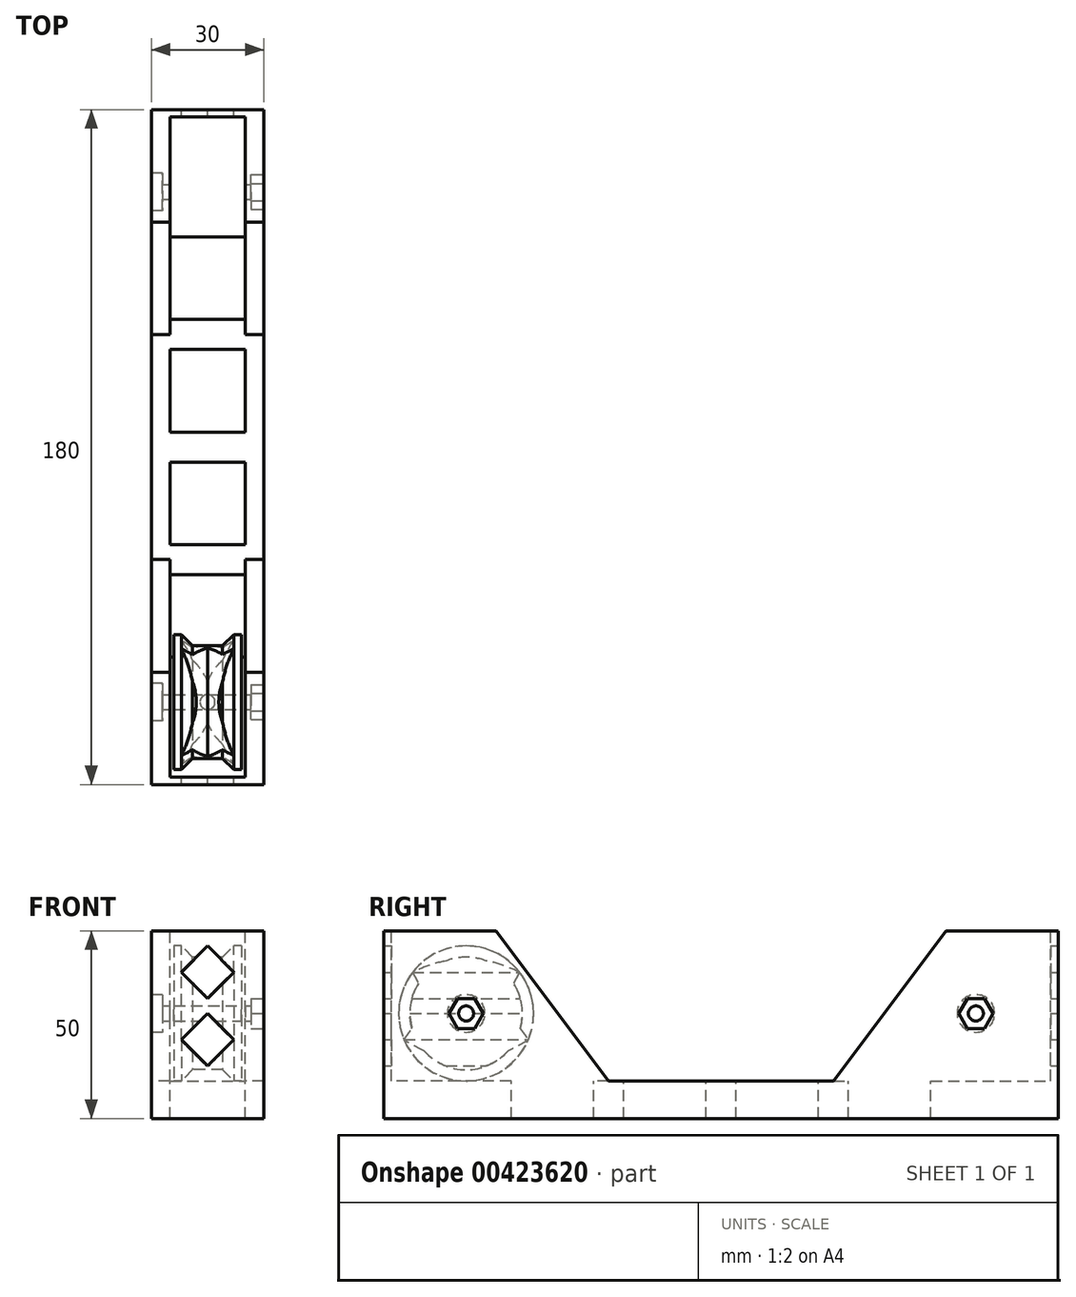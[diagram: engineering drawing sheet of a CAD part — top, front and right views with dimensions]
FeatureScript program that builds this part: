
annotation { "Feature Type Name" : "Feature", "Feature Type Description" : "" }
export const myFeature = defineFeature(function(context is Context, id is Id, definition is map)
    precondition{}
    {
        {
            var Q0;
            Q0=qCreatedBy(makeId("Right.planeOp"),FACE);
            var sketch = newSketch(context, id + "F0", { "sketchPlane" : qUnion([Q0])});
            skLineSegment(sketch, "E0", {"start": v(0, 0) * mm, "end": v(-90, 0) * mm});
            skLineSegment(sketch, "E1", {"start": v(-90, 0) * mm, "end": v(-90, 50) * mm});
            skLineSegment(sketch, "E2", {"start": v(-90, 50) * mm, "end": v(-60, 50) * mm});
            skLineSegment(sketch, "E3", {"start": v(-60, 50) * mm, "end": v(-30, 10) * mm});
            skLineSegment(sketch, "E4", {"start": v(-30, 10) * mm, "end": v(0, 10) * mm});
            skLineSegment(sketch, "E5.MirrorCS", {"start": v(30, 10) * mm, "end": v(0, 10) * mm});
            skLineSegment(sketch, "E6.MirrorCS", {"start": v(0, 0) * mm, "end": v(90, 0) * mm});
            skLineSegment(sketch, "E7.MirrorCS", {"start": v(90, 0) * mm, "end": v(90, 50) * mm});
            skLineSegment(sketch, "E8.MirrorCS", {"start": v(90, 50) * mm, "end": v(60, 50) * mm});
            skLineSegment(sketch, "E9.MirrorCS", {"start": v(60, 50) * mm, "end": v(30, 10) * mm});
            skPoint(sketch, "E10", {"position": v(-68, 28) * mm});
            skLineSegment(sketch, "E11", {"start": v(-68, 50) * mm, "end": v(-68, 0) * mm, "construction": true});
            skPoint(sketch, "E12.MirrorP", {"position": v(68, 28) * mm});
            skCircle(sketch, "E13", {"center": v(0, 120.74) * mm, "radius": 100 * mm, "construction": true});
            skCircle(sketch, "E14", {"center": v(-68, 28) * mm, "radius": 15 * mm});
            skSolve(sketch);
        }
        {
            var Q0;
            Q0=makeQuery(id+"F0.imprint","IMPRINT",FACE,{"disambiguationData":[TD([[makeQuery(id+"F0.imprint","IMPRINT",EDGE,{"derivedFrom":sQuery(id+"F0.wireOp",EDGE,"E0")}),-1.0]])]});
            var Q1;
            Q1=makeQuery(id+"F0.imprint","IMPRINT",FACE,{"disambiguationData":[TD([[makeQuery(id+"F0.imprint","IMPRINT",EDGE,{"derivedFrom":sQuery(id+"F0.wireOp",EDGE,"E14")}),1.0]])]});
            extrude(context, id + "F1", {"entities" : qUnion([Q0, Q1]), "endBound" : BoundingType.SYMMETRIC, "depth" : 30 * mm, "offsetDistance" : 25 * mm});
        }
        {
            var Q0;
            Q0=makeQuery(id+"F1.opExtrude","SWEPT_FACE",FACE,{"disambiguationData":[OSD([sQuery(id+"F0.wireOp",EDGE,"E2")])]});
            var sketch = newSketch(context, id + "F2", { "sketchPlane" : qUnion([Q0])});
            skLineSegment(sketch, "E15", {"start": v(-10, -30) * mm, "end": v(-10, -88) * mm});
            skLineSegment(sketch, "E16.MirrorCS", {"start": v(10, -30) * mm, "end": v(10, -88) * mm});
            skLineSegment(sketch, "E17.MirrorCS", {"start": v(10, 30) * mm, "end": v(10, 88) * mm});
            skLineSegment(sketch, "E18.MirrorCS", {"start": v(-10, 30) * mm, "end": v(-10, 88) * mm});
            skLineSegment(sketch, "E19", {"start": v(-10, -30) * mm, "end": v(10, -30) * mm});
            skLineSegment(sketch, "E20", {"start": v(-10, -88) * mm, "end": v(-11, -88) * mm});
            skLineSegment(sketch, "E21.MirrorCS", {"start": v(-10, 30) * mm, "end": v(10, 30) * mm});
            skLineSegment(sketch, "E22.MirrorCS", {"start": v(-11, 88) * mm, "end": v(-10, 88) * mm});
            skLineSegment(sketch, "E23", {"start": v(-10, -88) * mm, "end": v(10, -88) * mm});
            skLineSegment(sketch, "E24.MirrorCS", {"start": v(-10, 88) * mm, "end": v(10, 88) * mm});
            skSolve(sketch);
        }
        {
            var Q0;
            {var subQ0=sQuery(id+"F2.wireOp",EDGE,"E19");Q0=makeQuery(id+"F2.imprint","IMPRINT",FACE,{"disambiguationData":[TD([[makeQuery(id+"F2.imprint","IMPRINT",EDGE,{"derivedFrom":subQ0}),-1.0]])]});}
            var Q1;
            {var subQ0=sQuery(id+"F2.wireOp",EDGE,"E20");Q1=makeQuery(id+"F2.imprint","IMPRINT",FACE,{"disambiguationData":[TD([[makeQuery(id+"F2.imprint","IMPRINT",EDGE,{"derivedFrom":subQ0}),-1.0]])]});}
            var Q2;
            Q2=makeQuery(id+"F1.opExtrude","SWEPT_FACE",FACE,{"disambiguationData":[OSD([sQuery(id+"F0.wireOp",EDGE,"E0"),sQuery(id+"F0.wireOp",EDGE,"E6.MirrorCS")])]});
            extrude(context, id + "F3", {"entities" : qUnion([Q0, Q1]), "operationType" : NewBodyOperationType.REMOVE, "endBound" : BoundingType.UP_TO_SURFACE, "oppositeDirection" : true, "depth" : 25 * mm, "endBoundEntityFace" : qUnion([Q2]), "hasOffset" : true, "offsetDistance" : 10 * mm});
        }
        {
            var Q0;
            Q0=makeQuery(id+"F2.imprint","IMPRINT",FACE,{"disambiguationData":[TD([[makeQuery(id+"F2.imprint","IMPRINT",EDGE,{"derivedFrom":sQuery(id+"F2.wireOp",EDGE,"E17.MirrorCS")}),1.0]])]});
            var Q1;
            {var subQ0=sQuery(id+"F2.wireOp",EDGE,"E23");Q1=makeQuery(id+"F2.imprint","IMPRINT",FACE,{"disambiguationData":[TD([[makeQuery(id+"F2.imprint","IMPRINT",EDGE,{"derivedFrom":subQ0}),1.0]])]});}
            var Q2;
            Q2=makeQuery(id+"F1.opExtrude","SWEPT_FACE",FACE,{"disambiguationData":[OSD([sQuery(id+"F0.wireOp",EDGE,"E0"),sQuery(id+"F0.wireOp",EDGE,"E6.MirrorCS")])]});
            extrude(context, id + "F4", {"entities" : qUnion([Q0, Q1]), "operationType" : NewBodyOperationType.REMOVE, "endBound" : BoundingType.UP_TO_SURFACE, "oppositeDirection" : true, "depth" : 25 * mm, "endBoundEntityFace" : qUnion([Q2]), "hasOffset" : true, "offsetDistance" : 10 * mm});
        }
        {
            var Q0;
            Q0=sQuery(id+"F0.wireOp",VERTEX,"E10");
            var Q1;
            Q1=makeQuery(id+"F1.opExtrude","SWEPT_FACE",FACE,{"disambiguationData":[OSD([sQuery(id+"F0.wireOp",EDGE,"E1")])]});
            cPlane(context, id + "F5", {"entities" : qUnion([Q0, Q1]), "cplaneType" : CPlaneType.PLANE_POINT, "offset" : 25 * mm, "width" : 150 * mm, "height" : 150 * mm});
        }
        {
            var Q0;
            Q0=qCreatedBy(id+"F5.planeOp",FACE);
            var sketch = newSketch(context, id + "F6", { "sketchPlane" : qUnion([Q0])});
            skLineSegment(sketch, "E25.0", {"start": v(0, 43) * mm, "end": v(0, 13) * mm, "construction": true});
            skLineSegment(sketch, "E26", {"start": v(0, 43) * mm, "end": v(-4, 43) * mm});
            skLineSegment(sketch, "E27", {"start": v(-4, 43) * mm, "end": v(-7, 46) * mm});
            skLineSegment(sketch, "E28", {"start": v(-7, 46) * mm, "end": v(-9, 46) * mm});
            skLineSegment(sketch, "E29", {"start": v(-9, 46) * mm, "end": v(-9, 28) * mm});
            skPoint(sketch, "E29.endSnap0", {"position": v(0, 28) * mm});
            skLineSegment(sketch, "E30.MirrorCS", {"start": v(0, 43) * mm, "end": v(4, 43) * mm});
            skLineSegment(sketch, "E31.MirrorCS", {"start": v(4, 43) * mm, "end": v(7, 46) * mm});
            skLineSegment(sketch, "E32.MirrorCS", {"start": v(7, 46) * mm, "end": v(9, 46) * mm});
            skLineSegment(sketch, "E33.MirrorCS", {"start": v(9, 46) * mm, "end": v(9, 28) * mm});
            skLineSegment(sketch, "E34", {"start": v(-9, 28) * mm, "end": v(0, 28) * mm});
            skLineSegment(sketch, "E35.MirrorCS", {"start": v(9, 28) * mm, "end": v(0, 28) * mm});
            skSolve(sketch);
        }
        {
            var Q0;
            Q0 = qSketchRegion(id + "F6", true);
            var Q1;
            Q1=sQuery(id+"F6.wireOp",EDGE,"E34");
            revolve(context, id + "F7", {"entities" : qUnion([Q0]), "axis" : qUnion([Q1]), "revolveType" : RevolveType.FULL});
        }
        {
            var Q0;
            Q0=makeQuery(id+"F1.opExtrude","CAP_FACE",FACE,{"disambiguationData":[OSD([sQuery(id+"F0.wireOp",EDGE,"E0"),sQuery(id+"F0.wireOp",EDGE,"E1"),sQuery(id+"F0.wireOp",EDGE,"E2"),sQuery(id+"F0.wireOp",EDGE,"E3"),sQuery(id+"F0.wireOp",EDGE,"E4"),sQuery(id+"F0.wireOp",EDGE,"E5.MirrorCS"),sQuery(id+"F0.wireOp",EDGE,"E6.MirrorCS"),sQuery(id+"F0.wireOp",EDGE,"E7.MirrorCS"),sQuery(id+"F0.wireOp",EDGE,"E8.MirrorCS"),sQuery(id+"F0.wireOp",EDGE,"E9.MirrorCS")])],"isStart":false});
            var sketch = newSketch(context, id + "F8", { "sketchPlane" : qUnion([Q0])});
            skPoint(sketch, "E36.0", {"position": v(-68, 28) * mm});
            skPoint(sketch, "E37.0", {"position": v(68, 28) * mm});
            skCircle(sketch, "E38.cCircle", {"center": v(-68, 28) * mm, "radius": 4 * mm, "construction": true});
            skLineSegment(sketch, "E38.0", {"start": v(-65.7, 24) * mm, "end": v(-70.3, 24) * mm});
            skLineSegment(sketch, "E38.1", {"start": v(-70.3, 24) * mm, "end": v(-72.62, 28) * mm});
            skLineSegment(sketch, "E38.2", {"start": v(-72.62, 28) * mm, "end": v(-70.3, 32) * mm});
            skLineSegment(sketch, "E38.3", {"start": v(-70.3, 32) * mm, "end": v(-65.7, 32) * mm});
            skLineSegment(sketch, "E38.4", {"start": v(-65.7, 32) * mm, "end": v(-63.38, 28) * mm});
            skLineSegment(sketch, "E38.5", {"start": v(-63.38, 28) * mm, "end": v(-65.7, 24) * mm});
            skPoint(sketch, "E38.0.midPoint", {"position": v(-68, 24) * mm});
            skLineSegment(sketch, "E39.MirrorCS", {"start": v(65.7, 32) * mm, "end": v(63.38, 28) * mm});
            skLineSegment(sketch, "E40.MirrorCS", {"start": v(70.3, 32) * mm, "end": v(65.7, 32) * mm});
            skLineSegment(sketch, "E41.MirrorCS", {"start": v(72.62, 28) * mm, "end": v(70.3, 32) * mm});
            skLineSegment(sketch, "E42.MirrorCS", {"start": v(70.3, 24) * mm, "end": v(72.62, 28) * mm});
            skLineSegment(sketch, "E43.MirrorCS", {"start": v(65.7, 24) * mm, "end": v(70.3, 24) * mm});
            skLineSegment(sketch, "E44.MirrorCS", {"start": v(63.38, 28) * mm, "end": v(65.7, 24) * mm});
            skSolve(sketch);
        }
        {
            var Q0;
            Q0=sQuery(id+"F8.wireOp",VERTEX,"E36.0");
            var Q1;
            Q1=sQuery(id+"F8.wireOp",VERTEX,"E37.0");
            var Q2;
            Q2=makeQuery(id+"F1.opExtrude","SWEPT_BODY",BODY,{"disambiguationData":[OSD([sQuery(id+"F0.wireOp",EDGE,"E0"),sQuery(id+"F0.wireOp",EDGE,"E1"),sQuery(id+"F0.wireOp",EDGE,"E2"),sQuery(id+"F0.wireOp",EDGE,"E3"),sQuery(id+"F0.wireOp",EDGE,"E4"),sQuery(id+"F0.wireOp",EDGE,"E5.MirrorCS"),sQuery(id+"F0.wireOp",EDGE,"E6.MirrorCS"),sQuery(id+"F0.wireOp",EDGE,"E7.MirrorCS"),sQuery(id+"F0.wireOp",EDGE,"E8.MirrorCS"),sQuery(id+"F0.wireOp",EDGE,"E9.MirrorCS")])]});
            var Q3;
            Q3=makeQuery(id+"F7.opRevolve","SWEPT_BODY",BODY,{"disambiguationData":[OSD([sQuery(id+"F6.wireOp",EDGE,"E26"),sQuery(id+"F6.wireOp",EDGE,"E27"),sQuery(id+"F6.wireOp",EDGE,"E28"),sQuery(id+"F6.wireOp",EDGE,"E29"),sQuery(id+"F6.wireOp",EDGE,"E30.MirrorCS"),sQuery(id+"F6.wireOp",EDGE,"E31.MirrorCS"),sQuery(id+"F6.wireOp",EDGE,"E32.MirrorCS"),sQuery(id+"F6.wireOp",EDGE,"E33.MirrorCS"),sQuery(id+"F6.wireOp",EDGE,"E34"),sQuery(id+"F6.wireOp",EDGE,"E35.MirrorCS")])]});
            hole(context, id + "F9", {"style" : HoleStyle.SIMPLE, "endStyle" : HoleEndStyle.THROUGH, "holeDiameter" : 4 * mm, "isTappedThrough" : true, "tappedDepth" : 6 * mm, "tapClearance" : 3, "locations" : qUnion([Q0, Q1]), "scope" : qUnion([Q2, Q3])});
        }
        {
            var Q0;
            {var subQ0=sQuery(id+"F0.wireOp",EDGE,"E6.MirrorCS");var subQ1=sQuery(id+"F0.wireOp",EDGE,"E0");Q0=makeQuery(id+"F4.boolean.opBoolean","MERGE",FACE,{"derivedFrom":[makeQuery(id+"F3.boolean.opBoolean","MERGE",FACE,{"derivedFrom":[makeQuery(id+"F1.opExtrude","SWEPT_FACE",FACE,{"disambiguationData":[OSD([sQuery(id+"F0.wireOp",EDGE,"E4"),sQuery(id+"F0.wireOp",EDGE,"E5.MirrorCS")])]}),makeQuery(id+"F3.opExtrude","CAP_FACE",FACE,{"disambiguationData":[OSD([subQ1,subQ0])],"isStart":false})]}),makeQuery(id+"F4.opExtrude","CAP_FACE",FACE,{"disambiguationData":[OSD([subQ1,subQ0])],"isStart":false})]});}
            var sketch = newSketch(context, id + "F10", { "sketchPlane" : qUnion([Q0])});
            skPoint(sketch, "E45.middle", {"position": v(0, 0) * mm});
            skLineSegment(sketch, "E46.bottom", {"start": v(-10, 26) * mm, "end": v(10, 26) * mm});
            skLineSegment(sketch, "E46.top", {"start": v(-10, 4) * mm, "end": v(10, 4) * mm});
            skLineSegment(sketch, "E46.left", {"start": v(-10, 26) * mm, "end": v(-10, 4) * mm});
            skLineSegment(sketch, "E46.right", {"start": v(10, 26) * mm, "end": v(10, 4) * mm});
            skPoint(sketch, "E46.middle", {"position": v(0, 15) * mm});
            skLineSegment(sketch, "E47.MirrorCS", {"start": v(-10, -4) * mm, "end": v(10, -4) * mm});
            skLineSegment(sketch, "E48.MirrorCS", {"start": v(10, -26) * mm, "end": v(10, -4) * mm});
            skLineSegment(sketch, "E49.MirrorCS", {"start": v(-10, -26) * mm, "end": v(10, -26) * mm});
            skLineSegment(sketch, "E50.MirrorCS", {"start": v(-10, -26) * mm, "end": v(-10, -4) * mm});
            skLineSegment(sketch, "E51", {"start": v(15, -30) * mm, "end": v(-15, -30) * mm, "construction": true});
            skLineSegment(sketch, "E52.MirrorCS", {"start": v(-10, -34) * mm, "end": v(10, -34) * mm});
            skLineSegment(sketch, "E53.MirrorCS", {"start": v(10, -34) * mm, "end": v(10, -56) * mm});
            skLineSegment(sketch, "E54.MirrorCS", {"start": v(-10, -56) * mm, "end": v(10, -56) * mm});
            skLineSegment(sketch, "E55.MirrorCS", {"start": v(-10, -34) * mm, "end": v(-10, -56) * mm});
            skLineSegment(sketch, "E56.MirrorCS", {"start": v(-10, 34) * mm, "end": v(10, 34) * mm});
            skLineSegment(sketch, "E57.MirrorCS", {"start": v(-10, 56) * mm, "end": v(10, 56) * mm});
            skLineSegment(sketch, "E58.MirrorCS", {"start": v(10, 34) * mm, "end": v(10, 56) * mm});
            skLineSegment(sketch, "E59.MirrorCS", {"start": v(-10, 34) * mm, "end": v(-10, 56) * mm});
            skSolve(sketch);
        }
        {
            var Q0;
            Q0 = qSketchRegion(id + "F10", true);
            var Q1;
            Q1=makeQuery(id+"F1.opExtrude","SWEPT_FACE",FACE,{"disambiguationData":[OSD([sQuery(id+"F0.wireOp",EDGE,"E0"),sQuery(id+"F0.wireOp",EDGE,"E6.MirrorCS")])]});
            extrude(context, id + "F11", {"entities" : qUnion([Q0]), "operationType" : NewBodyOperationType.REMOVE, "endBound" : BoundingType.UP_TO_SURFACE, "oppositeDirection" : true, "depth" : 25 * mm, "endBoundEntityFace" : qUnion([Q1]), "offsetDistance" : 25 * mm});
        }
        {
            var Q0;
            Q0=makeQuery(id+"F8.imprint","IMPRINT",FACE,{"disambiguationData":[TD([[makeQuery(id+"F8.imprint","IMPRINT",EDGE,{"derivedFrom":sQuery(id+"F8.wireOp",EDGE,"E38.0")}),-1.0]])]});
            var Q1;
            Q1=makeQuery(id+"F8.imprint","IMPRINT",FACE,{"disambiguationData":[TD([[makeQuery(id+"F8.imprint","IMPRINT",EDGE,{"derivedFrom":sQuery(id+"F8.wireOp",EDGE,"E39.MirrorCS")}),1.0]])]});
            var Q2;
            {var subQ0=sQuery(id+"F2.wireOp",EDGE,"E16.MirrorCS");Q2=makeQuery(id+"F4.boolean.opBoolean","MERGE",FACE,{"derivedFrom":[makeQuery(id+"F3.boolean.opBoolean","COPY",FACE,{"derivedFrom":makeQuery(id+"F3.opExtrude","SWEPT_FACE",FACE,{"disambiguationData":[OSD([subQ0])]})}),makeQuery(id+"F4.opExtrude","SWEPT_FACE",FACE,{"disambiguationData":[OSD([subQ0])]})]});}
            extrude(context, id + "F12", {"entities" : qUnion([Q0, Q1]), "operationType" : NewBodyOperationType.REMOVE, "endBound" : BoundingType.UP_TO_SURFACE, "oppositeDirection" : true, "depth" : 25 * mm, "endBoundEntityFace" : qUnion([Q2]), "hasOffset" : true, "offsetDistance" : 1.6 * mm});
        }
        {
            var Q0;
            Q0=makeQuery(id+"F1.opExtrude","CAP_FACE",FACE,{"disambiguationData":[OSD([sQuery(id+"F0.wireOp",EDGE,"E0"),sQuery(id+"F0.wireOp",EDGE,"E1"),sQuery(id+"F0.wireOp",EDGE,"E2"),sQuery(id+"F0.wireOp",EDGE,"E3"),sQuery(id+"F0.wireOp",EDGE,"E4"),sQuery(id+"F0.wireOp",EDGE,"E5.MirrorCS"),sQuery(id+"F0.wireOp",EDGE,"E6.MirrorCS"),sQuery(id+"F0.wireOp",EDGE,"E7.MirrorCS"),sQuery(id+"F0.wireOp",EDGE,"E8.MirrorCS"),sQuery(id+"F0.wireOp",EDGE,"E9.MirrorCS")])],"isStart":true});
            var sketch = newSketch(context, id + "F13", { "sketchPlane" : qUnion([Q0])});
            skCircle(sketch, "E60", {"center": v(68, 28) * mm, "radius": 5 * mm});
            skCircle(sketch, "E61.MirrorC", {"center": v(-68, 28) * mm, "radius": 5 * mm});
            skSolve(sketch);
        }
        {
            var Q0;
            Q0 = qSketchRegion(id + "F13", true);
            extrude(context, id + "F14", {"entities" : qUnion([Q0]), "operationType" : NewBodyOperationType.REMOVE, "oppositeDirection" : true, "depth" : 3 * mm, "offsetDistance" : 25 * mm});
        }
        {
            var Q0;
            Q0=makeQuery(id+"F1.opExtrude","SWEPT_FACE",FACE,{"disambiguationData":[OSD([sQuery(id+"F0.wireOp",EDGE,"E7.MirrorCS")])]});
            var sketch = newSketch(context, id + "F15", { "sketchPlane" : qUnion([Q0])});
            skLineSegment(sketch, "E62.0", {"start": v(-10, 10) * mm, "end": v(-10, 50) * mm, "construction": true});
            skLineSegment(sketch, "E63.0", {"start": v(10, 10) * mm, "end": v(10, 50) * mm, "construction": true});
            skLineSegment(sketch, "E64", {"start": v(-10, 30) * mm, "end": v(10, 30) * mm, "construction": true});
            skLineSegment(sketch, "E65", {"start": v(0, 32) * mm, "end": v(-7, 39) * mm});
            skLineSegment(sketch, "E66", {"start": v(-7, 39) * mm, "end": v(0, 46) * mm});
            skLineSegment(sketch, "E67", {"start": v(0, 46) * mm, "end": v(7, 39) * mm});
            skLineSegment(sketch, "E68", {"start": v(7, 39) * mm, "end": v(0, 32) * mm});
            skLineSegment(sketch, "E69.MirrorCS", {"start": v(0, 28) * mm, "end": v(-7, 21) * mm});
            skLineSegment(sketch, "E70.MirrorCS", {"start": v(7, 21) * mm, "end": v(0, 28) * mm});
            skLineSegment(sketch, "E71.MirrorCS", {"start": v(0, 14) * mm, "end": v(7, 21) * mm});
            skLineSegment(sketch, "E72.MirrorCS", {"start": v(-7, 21) * mm, "end": v(0, 14) * mm});
            skSolve(sketch);
        }
        {
            var Q0;
            Q0=makeQuery(id+"F15.imprint","IMPRINT",FACE,{"disambiguationData":[TD([[makeQuery(id+"F15.imprint","IMPRINT",EDGE,{"derivedFrom":sQuery(id+"F15.wireOp",EDGE,"E65")}),-1.0]])]});
            var Q1;
            Q1=makeQuery(id+"F15.imprint","IMPRINT",FACE,{"disambiguationData":[TD([[makeQuery(id+"F15.imprint","IMPRINT",EDGE,{"derivedFrom":sQuery(id+"F15.wireOp",EDGE,"E69.MirrorCS")}),1.0]])]});
            var Q2;
            Q2=makeQuery(id+"F4.boolean.opBoolean","COPY",FACE,{"derivedFrom":makeQuery(id+"F4.opExtrude","SWEPT_FACE",FACE,{"disambiguationData":[OSD([sQuery(id+"F2.wireOp",EDGE,"E24.MirrorCS")])]})});
            extrude(context, id + "F16", {"entities" : qUnion([Q0, Q1]), "operationType" : NewBodyOperationType.REMOVE, "endBound" : BoundingType.THROUGH_ALL, "oppositeDirection" : true, "depth" : 25 * mm, "endBoundEntityFace" : qUnion([Q2]), "offsetDistance" : 25 * mm});
        }
    });
